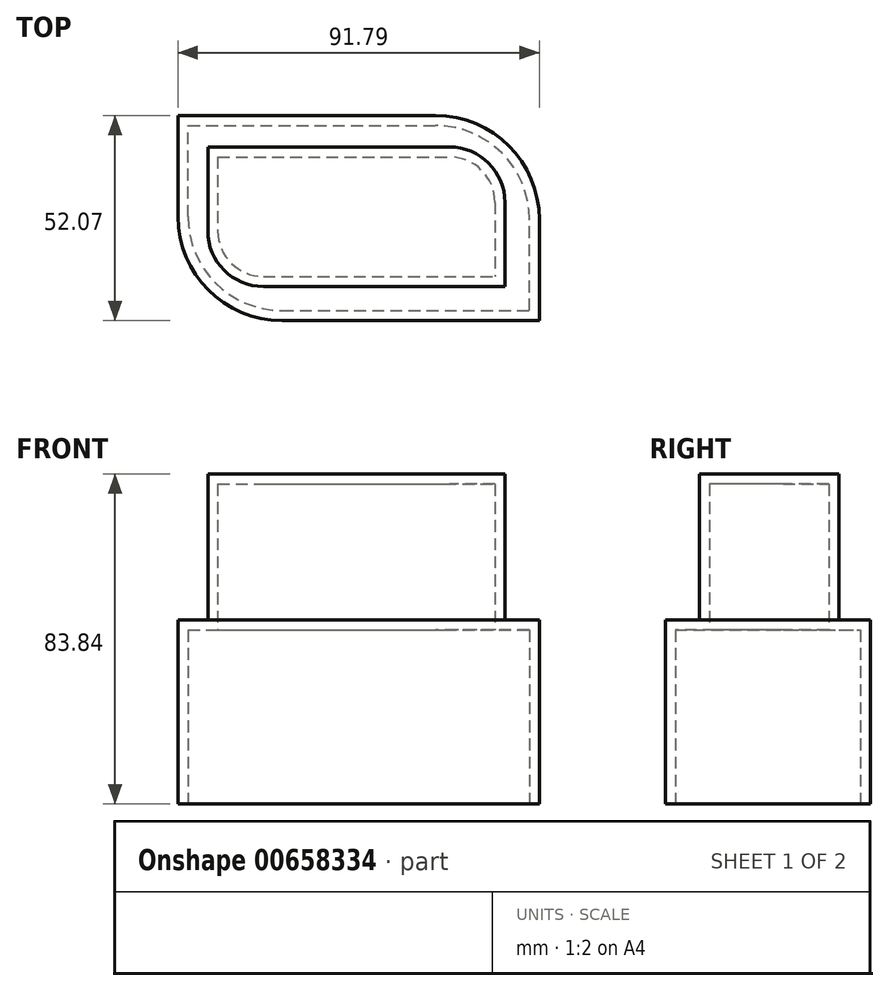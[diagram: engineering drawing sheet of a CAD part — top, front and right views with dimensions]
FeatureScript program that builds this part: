
annotation { "Feature Type Name" : "Feature", "Feature Type Description" : "" }
export const myFeature = defineFeature(function(context is Context, id is Id, definition is map)
    precondition{}
    {
        {
            var Q0;
            Q0=qCreatedBy(makeId("Front.planeOp"),FACE);
            var sketch = newSketch(context, id + "F0", { "sketchPlane" : qUnion([Q0])});
            skLineSegment(sketch, "E0.bottom", {"start": v(-75.4, 50.47) * mm, "end": v(16.4, 50.47) * mm});
            skLineSegment(sketch, "E0.top", {"start": v(-75.4, 3.71) * mm, "end": v(16.4, 3.71) * mm});
            skLineSegment(sketch, "E0.left", {"start": v(-75.4, 50.47) * mm, "end": v(-75.4, 3.71) * mm});
            skLineSegment(sketch, "E0.right", {"start": v(16.4, 50.47) * mm, "end": v(16.4, 3.71) * mm});
            skSolve(sketch);
        }
        {
            var Q0;
            Q0=makeQuery(id+"F0.imprint","IMPRINT",FACE,{"disambiguationData":[TD([[makeQuery(id+"F0.imprint","IMPRINT",EDGE,{"derivedFrom":sQuery(id+"F0.wireOp",EDGE,"E0.bottom")}),-1.0]])]});
            extrude(context, id + "F1", {"entities" : qUnion([Q0]), "depth" : 52.07 * mm, "offsetDistance" : 25.4 * mm});
        }
        {
            var Q0;
            Q0=makeQuery(id+"F1.opExtrude","CAP_EDGE",EDGE,{"disambiguationData":[OSD([sQuery(id+"F0.wireOp",EDGE,"E0.left")])],"isStart":false});
            var Q1;
            Q1=makeQuery(id+"F1.opExtrude","CAP_EDGE",EDGE,{"disambiguationData":[OSD([sQuery(id+"F0.wireOp",EDGE,"E0.right")])],"isStart":true});
            fillet(context, id + "F2", {"entities" : qUnion([Q0, Q1]), "radius" : 26.37 * mm, "tangentPropagation" : true, "allowEdgeOverflow" : false});
        }
        {
            var Q0;
            Q0=makeQuery(id+"F1.opExtrude","SWEPT_FACE",FACE,{"disambiguationData":[OSD([sQuery(id+"F0.wireOp",EDGE,"E0.bottom")])]});
            var sketch = newSketch(context, id + "F3", { "sketchPlane" : qUnion([Q0])});
            skLineSegment(sketch, "E1.bottom", {"start": v(-67.82, -7.97) * mm, "end": v(7.66, -7.97) * mm});
            skLineSegment(sketch, "E1.top", {"start": v(-67.82, -43.43) * mm, "end": v(7.66, -43.43) * mm});
            skLineSegment(sketch, "E1.left", {"start": v(-67.82, -7.97) * mm, "end": v(-67.82, -43.43) * mm});
            skLineSegment(sketch, "E1.right", {"start": v(7.66, -7.97) * mm, "end": v(7.66, -43.43) * mm});
            skSolve(sketch);
        }
        {
            var Q0;
            Q0=makeQuery(id+"F3.imprint","IMPRINT",FACE,{"disambiguationData":[TD([[makeQuery(id+"F3.imprint","IMPRINT",EDGE,{"derivedFrom":sQuery(id+"F3.wireOp",EDGE,"E1.bottom")}),-1.0]])]});
            extrude(context, id + "F4", {"entities" : qUnion([Q0]), "operationType" : NewBodyOperationType.ADD, "depth" : 25.4 * mm, "offsetDistance" : 25.4 * mm});
        }
        {
            var Q0;
            Q0=makeQuery(id+"F4.opExtrude","CAP_FACE",FACE,{"disambiguationData":[OSD([sQuery(id+"F3.wireOp",EDGE,"E1.bottom"),sQuery(id+"F3.wireOp",EDGE,"E1.top"),sQuery(id+"F3.wireOp",EDGE,"E1.left"),sQuery(id+"F3.wireOp",EDGE,"E1.right")])],"isStart":false});
            extrude(context, id + "F5", {"entities" : qUnion([Q0]), "operationType" : NewBodyOperationType.ADD, "depth" : 11.68 * mm, "offsetDistance" : 25.4 * mm});
        }
        {
            var Q0;
            {var subQ0=sQuery(id+"F3.wireOp",EDGE,"E1.left");var subQ1=sQuery(id+"F3.wireOp",EDGE,"E1.top");Q0=makeQuery(id+"F5.boolean.opBoolean","MERGE",EDGE,{"derivedFrom":[makeQuery(id+"F4.opExtrude","SWEPT_EDGE",EDGE,{"disambiguationData":[OSD([subQ1,subQ0])]}),makeQuery(id+"F5.opExtrude","SWEPT_EDGE",EDGE,{"disambiguationData":[OSD([subQ1,subQ0])]})]});}
            fillet(context, id + "F6", {"entities" : qUnion([Q0]), "radius" : 14.1 * mm, "tangentPropagation" : true, "allowEdgeOverflow" : false});
        }
        {
            var Q0;
            {var subQ0=sQuery(id+"F3.wireOp",EDGE,"E1.right");var subQ1=sQuery(id+"F3.wireOp",EDGE,"E1.bottom");Q0=makeQuery(id+"F5.boolean.opBoolean","MERGE",EDGE,{"derivedFrom":[makeQuery(id+"F4.opExtrude","SWEPT_EDGE",EDGE,{"disambiguationData":[OSD([subQ1,subQ0])]}),makeQuery(id+"F5.opExtrude","SWEPT_EDGE",EDGE,{"disambiguationData":[OSD([subQ1,subQ0])]})]});}
            fillet(context, id + "F7", {"entities" : qUnion([Q0]), "radius" : 14.1 * mm, "tangentPropagation" : true, "allowEdgeOverflow" : false});
        }
        {
            var Q0;
            Q0=makeQuery(id+"F1.opExtrude","SWEPT_FACE",FACE,{"disambiguationData":[OSD([sQuery(id+"F0.wireOp",EDGE,"E0.top")])]});
            shell(context, id + "F8", {"entities" : qUnion([Q0]), "thickness" : 2.54 * mm});
        }
    });
